# Revit family: QF_ELECTROLUXPROFESSIONAL_1LSN93_WH6-11_S
name_source: partatom
category: Attrezzature speciali
units: mm (PartAtom-declared; Revit-internal decimal feet)

## family parameters
Basato su piano di lavoro = No
Condiviso = No
Punto di calcolo locali = No
Quota connettore circolare = Usa diametro
Sempre verticale = Sì
Taglio con vuoti quando caricato = No
Tipo di parte = Normale

## types (3) — shared parameters
Cycle = 50 Hz
Depth Actual = 766 mm  [stored 2.51312 ft]
Height Actual = 1212 mm  [stored 3.97638 ft]
Latent Heat Output = 0.0
Length Actual = 830 mm  [stored 2.7231 ft]
Modello = WH6-11
Produttore = Electrolux Professional
Sensible Heat Output = 0.0
URL = www.electroluxprofessional.com
Watts = 1100 W
Weight = 202
zero-valued in all types: Gas KW, Prospetto di default, Steam Pounds per Hour

## per-type parameters (varying)
| type | Descrizione | Item Number | Phase | Volts |
| 9867730172 | WASHER WH6-11 11KG STEAM 200/50/60/3 COMPASS PRO 6H43 JP,EN 2xWATER POWDER+5xLIQ. VALV.OPEN SILVER 2.I/O DISCON. | 1L0GRH | 3 | 200 V |
| 9867730115 | WASHER WH6-11 11KG STEAM 200/50/60/3 COMPASS PRO 6H43 JP,EN 2xWATER POWDER+5xLIQ. VALV.OPEN SST/SILVER 2.I/O DISCON. | 1LA1AD | 3 | 200 V |
| 9867730118 | WASHER WH6-11 11KG STEAM 220-240/50/1N COMPASS PRO 6G01 ML 2xWATER POWDER+5xLIQ. VALV.OPEN SILVER 2.I/O DISCON. STOP | 1LA1AY | 1 | 240 V |

note: [stored X ft] marks values corroborated as IEEE doubles in the binary element streams (Revit-internal decimal feet)

## geometry (parser evidence)
native form markers: Blend x4
no freeform markers — native parametric forms only
